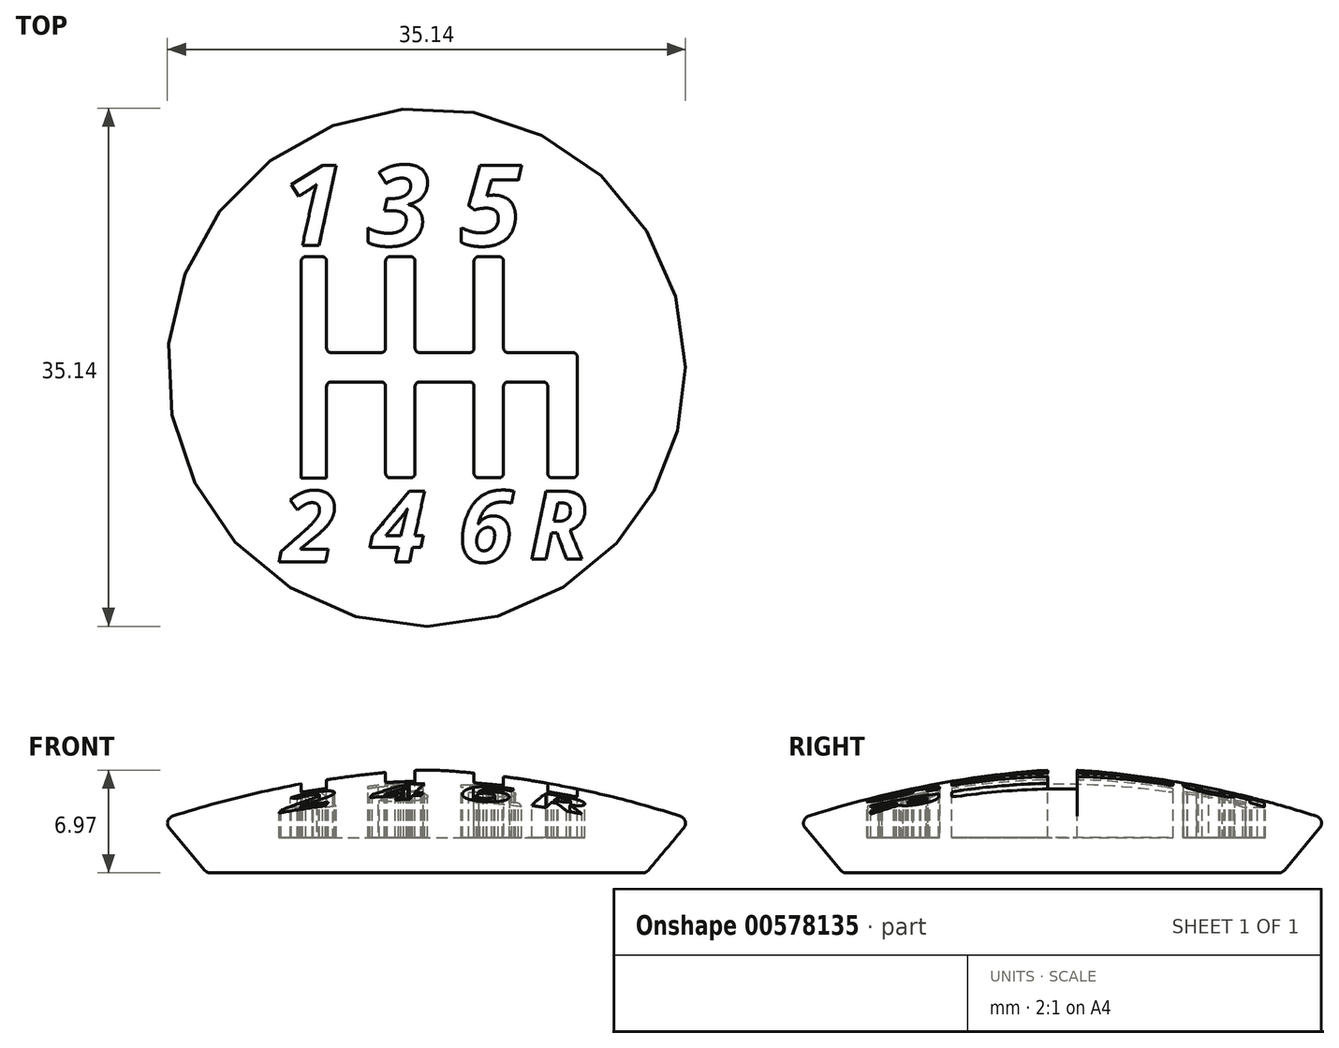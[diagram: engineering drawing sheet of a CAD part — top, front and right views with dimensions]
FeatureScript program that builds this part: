
annotation { "Feature Type Name" : "Feature", "Feature Type Description" : "" }
export const myFeature = defineFeature(function(context is Context, id is Id, definition is map)
    precondition{}
    {
        {
            var Q0;
            Q0=qCreatedBy(makeId("Front.planeOp"),FACE);
            var sketch = newSketch(context, id + "F0", { "sketchPlane" : qUnion([Q0])});
            skLineSegment(sketch, "E0", {"start": v(0, 0) * mm, "end": v(0, 7.03) * mm});
            skLineSegment(sketch, "E1", {"start": v(0, 0) * mm, "end": v(-14.9, 0) * mm});
            skLineSegment(sketch, "E2", {"start": v(-14.9, 0) * mm, "end": v(-17.93, 3.61) * mm});
            skArc(sketch, "E3", {"start": v(0, 7.03) * mm, "mid": v(-9.08, 5.93) * mm, "end": v(-17.93, 3.61) * mm});
            skPoint(sketch, "E3.third.point", {"position": v(25.22, 3.61) * mm});
            skLineSegment(sketch, "E4", {"start": v(-17.93, 3.61) * mm, "end": v(-17.93, 14.45) * mm, "construction": true});
            skSolve(sketch);
        }
        {
            var Q0;
            Q0=makeQuery(id+"F0.imprint","IMPRINT",FACE,{"disambiguationData":[TD([[makeQuery(id+"F0.imprint","IMPRINT",EDGE,{"derivedFrom":sQuery(id+"F0.wireOp",EDGE,"E0")}),1.0]])]});
            var Q1;
            Q1=sQuery(id+"F0.wireOp",EDGE,"E0");
            revolve(context, id + "F1", {"entities" : qUnion([Q0]), "axis" : qUnion([Q1]), "revolveType" : RevolveType.FULL});
        }
        {
            var Q0;
            Q0=qCreatedBy(makeId("Top.planeOp"),FACE);
            cPlane(context, id + "F2", {"entities" : qUnion([Q0]), "cplaneType" : CPlaneType.OFFSET, "offset" : 24.9 * mm, "width" : 152.4 * mm, "height" : 152.4 * mm});
        }
        {
            var Q0;
            Q0=qCreatedBy(id+"F2.planeOp",FACE);
            var sketch = newSketch(context, id + "F3", { "sketchPlane" : qUnion([Q0])});
            skLineSegment(sketch, "E5", {"start": v(-8.5, 7.2) * mm, "end": v(-8.5, -7.5) * mm});
            skLineSegment(sketch, "E6", {"start": v(-9.44, -7.5) * mm, "end": v(-6.78, -7.5) * mm});
            skLineSegment(sketch, "E7", {"start": v(-6.78, -7.5) * mm, "end": v(-6.78, -1.3) * mm});
            skLineSegment(sketch, "E8", {"start": v(-6.48, -1) * mm, "end": v(-3.08, -1) * mm});
            skLineSegment(sketch, "E9", {"start": v(-2.78, -1.3) * mm, "end": v(-2.78, -7.2) * mm});
            skLineSegment(sketch, "E10", {"start": v(-2.48, -7.5) * mm, "end": v(-1.08, -7.5) * mm});
            skLineSegment(sketch, "E11", {"start": v(-0.78, -7.2) * mm, "end": v(-0.78, -1.3) * mm});
            skLineSegment(sketch, "E12", {"start": v(-0.48, -1) * mm, "end": v(2.92, -1) * mm});
            skLineSegment(sketch, "E13", {"start": v(3.22, -1.3) * mm, "end": v(3.22, -7.2) * mm});
            skLineSegment(sketch, "E14", {"start": v(3.52, -7.5) * mm, "end": v(4.92, -7.5) * mm});
            skLineSegment(sketch, "E15", {"start": v(5.22, -7.2) * mm, "end": v(5.22, -1.3) * mm});
            skLineSegment(sketch, "E16", {"start": v(5.52, -1) * mm, "end": v(7.92, -1) * mm});
            skLineSegment(sketch, "E17", {"start": v(8.22, -1.3) * mm, "end": v(8.22, -7.2) * mm});
            skLineSegment(sketch, "E18", {"start": v(8.52, -7.5) * mm, "end": v(9.92, -7.5) * mm});
            skLineSegment(sketch, "E19", {"start": v(10.22, -7.2) * mm, "end": v(10.22, 0.7) * mm});
            skLineSegment(sketch, "E20", {"start": v(9.92, 1) * mm, "end": v(5.52, 1) * mm});
            skLineSegment(sketch, "E21", {"start": v(5.22, 1.3) * mm, "end": v(5.22, 7.2) * mm});
            skLineSegment(sketch, "E22", {"start": v(4.92, 7.5) * mm, "end": v(3.52, 7.5) * mm});
            skLineSegment(sketch, "E23", {"start": v(3.22, 7.2) * mm, "end": v(3.22, 1.3) * mm});
            skLineSegment(sketch, "E24", {"start": v(2.92, 1) * mm, "end": v(-0.48, 1) * mm});
            skLineSegment(sketch, "E25", {"start": v(-0.78, 1.3) * mm, "end": v(-0.78, 7.2) * mm});
            skLineSegment(sketch, "E26", {"start": v(-1.08, 7.5) * mm, "end": v(-2.48, 7.5) * mm});
            skLineSegment(sketch, "E27", {"start": v(-2.78, 7.2) * mm, "end": v(-2.78, 1.3) * mm});
            skLineSegment(sketch, "E28", {"start": v(-3.08, 1) * mm, "end": v(-6.48, 1) * mm});
            skLineSegment(sketch, "E29", {"start": v(-6.78, 1.3) * mm, "end": v(-6.78, 7.2) * mm});
            skLineSegment(sketch, "E30", {"start": v(-7.08, 7.5) * mm, "end": v(-8.2, 7.5) * mm});
            skPoint(sketch, "E31.visualSharp", {"position": v(-8.78, 7.5) * mm});
            skArc(sketch, "E31.filletArc", {"start": v(-8.2, 7.5) * mm, "mid": v(-8.4, 7.41) * mm, "end": v(-8.5, 7.2) * mm});
            skPoint(sketch, "E32.visualSharp", {"position": v(-6.78, 7.5) * mm});
            skArc(sketch, "E32.filletArc", {"start": v(-6.78, 7.2) * mm, "mid": v(-6.86, 7.41) * mm, "end": v(-7.08, 7.5) * mm});
            skPoint(sketch, "E33.visualSharp", {"position": v(-6.78, 1) * mm});
            skArc(sketch, "E33.filletArc", {"start": v(-6.78, 1.3) * mm, "mid": v(-6.69, 1.09) * mm, "end": v(-6.48, 1) * mm});
            skPoint(sketch, "E34.visualSharp", {"position": v(-2.78, 1) * mm});
            skArc(sketch, "E34.filletArc", {"start": v(-3.08, 1) * mm, "mid": v(-2.86, 1.09) * mm, "end": v(-2.78, 1.3) * mm});
            skPoint(sketch, "E35.visualSharp", {"position": v(-2.78, 7.5) * mm});
            skArc(sketch, "E35.filletArc", {"start": v(-2.48, 7.5) * mm, "mid": v(-2.69, 7.41) * mm, "end": v(-2.78, 7.2) * mm});
            skPoint(sketch, "E36.visualSharp", {"position": v(-0.78, 7.5) * mm});
            skArc(sketch, "E36.filletArc", {"start": v(-0.78, 7.2) * mm, "mid": v(-0.86, 7.41) * mm, "end": v(-1.08, 7.5) * mm});
            skPoint(sketch, "E37.visualSharp", {"position": v(-0.78, 1) * mm});
            skArc(sketch, "E37.filletArc", {"start": v(-0.78, 1.3) * mm, "mid": v(-0.69, 1.09) * mm, "end": v(-0.48, 1) * mm});
            skPoint(sketch, "E38.visualSharp", {"position": v(3.22, 1) * mm});
            skArc(sketch, "E38.filletArc", {"start": v(2.92, 1) * mm, "mid": v(3.14, 1.09) * mm, "end": v(3.22, 1.3) * mm});
            skPoint(sketch, "E39.visualSharp", {"position": v(3.22, 7.5) * mm});
            skArc(sketch, "E39.filletArc", {"start": v(3.52, 7.5) * mm, "mid": v(3.31, 7.41) * mm, "end": v(3.22, 7.2) * mm});
            skPoint(sketch, "E40.visualSharp", {"position": v(5.22, 7.5) * mm});
            skArc(sketch, "E40.filletArc", {"start": v(5.22, 7.2) * mm, "mid": v(5.14, 7.41) * mm, "end": v(4.92, 7.5) * mm});
            skPoint(sketch, "E41.visualSharp", {"position": v(5.22, 1) * mm});
            skArc(sketch, "E41.filletArc", {"start": v(5.22, 1.3) * mm, "mid": v(5.31, 1.09) * mm, "end": v(5.52, 1) * mm});
            skPoint(sketch, "E42.visualSharp", {"position": v(10.22, 1) * mm});
            skArc(sketch, "E42.filletArc", {"start": v(10.22, 0.7) * mm, "mid": v(10.14, 0.91) * mm, "end": v(9.92, 1) * mm});
            skPoint(sketch, "E43.visualSharp", {"position": v(10.22, -7.5) * mm});
            skArc(sketch, "E43.filletArc", {"start": v(9.92, -7.5) * mm, "mid": v(10.14, -7.41) * mm, "end": v(10.22, -7.2) * mm});
            skPoint(sketch, "E44.visualSharp", {"position": v(8.22, -7.5) * mm});
            skArc(sketch, "E44.filletArc", {"start": v(8.22, -7.2) * mm, "mid": v(8.31, -7.41) * mm, "end": v(8.52, -7.5) * mm});
            skPoint(sketch, "E45.visualSharp", {"position": v(8.22, -1) * mm});
            skArc(sketch, "E45.filletArc", {"start": v(8.22, -1.3) * mm, "mid": v(8.14, -1.09) * mm, "end": v(7.92, -1) * mm});
            skPoint(sketch, "E46.visualSharp", {"position": v(5.22, -1) * mm});
            skArc(sketch, "E46.filletArc", {"start": v(5.52, -1) * mm, "mid": v(5.31, -1.09) * mm, "end": v(5.22, -1.3) * mm});
            skPoint(sketch, "E47.visualSharp", {"position": v(5.22, -7.5) * mm});
            skArc(sketch, "E47.filletArc", {"start": v(4.92, -7.5) * mm, "mid": v(5.14, -7.41) * mm, "end": v(5.22, -7.2) * mm});
            skPoint(sketch, "E48.visualSharp", {"position": v(3.22, -7.5) * mm});
            skArc(sketch, "E48.filletArc", {"start": v(3.22, -7.2) * mm, "mid": v(3.31, -7.41) * mm, "end": v(3.52, -7.5) * mm});
            skPoint(sketch, "E49.visualSharp", {"position": v(3.22, -1) * mm});
            skArc(sketch, "E49.filletArc", {"start": v(3.22, -1.3) * mm, "mid": v(3.14, -1.09) * mm, "end": v(2.92, -1) * mm});
            skPoint(sketch, "E50.visualSharp", {"position": v(-0.78, -1) * mm});
            skArc(sketch, "E50.filletArc", {"start": v(-0.48, -1) * mm, "mid": v(-0.69, -1.09) * mm, "end": v(-0.78, -1.3) * mm});
            skPoint(sketch, "E51.visualSharp", {"position": v(-0.78, -7.5) * mm});
            skArc(sketch, "E51.filletArc", {"start": v(-1.08, -7.5) * mm, "mid": v(-0.86, -7.41) * mm, "end": v(-0.78, -7.2) * mm});
            skPoint(sketch, "E52.visualSharp", {"position": v(-2.78, -7.5) * mm});
            skArc(sketch, "E52.filletArc", {"start": v(-2.78, -7.2) * mm, "mid": v(-2.69, -7.41) * mm, "end": v(-2.48, -7.5) * mm});
            skPoint(sketch, "E53.visualSharp", {"position": v(-2.78, -1) * mm});
            skArc(sketch, "E53.filletArc", {"start": v(-2.78, -1.3) * mm, "mid": v(-2.86, -1.09) * mm, "end": v(-3.08, -1) * mm});
            skPoint(sketch, "E54.visualSharp", {"position": v(-6.78, -1) * mm});
            skArc(sketch, "E54.filletArc", {"start": v(-6.48, -1) * mm, "mid": v(-6.69, -1.09) * mm, "end": v(-6.78, -1.3) * mm});
            skPoint(sketch, "E55.visualSharp", {"position": v(-6.78, -7.5) * mm});
            skArc(sketch, "E55.filletArc", {"start": v(-6.78, -7.5) * mm, "mid": v(-7.37, -7.46) * mm, "end": v(-6.8, -7.6) * mm});
            skPoint(sketch, "E56.visualSharp", {"position": v(-8.2, -7.5) * mm});
            skArc(sketch, "E56.filletArc", {"start": v(-8.5, -7.5) * mm, "mid": v(-8.37, -7.5) * mm, "end": v(-8.25, -7.44) * mm});
            skLineSegment(sketch, "E57", {"start": v(-19.99, 0) * mm, "end": v(21.16, 0) * mm, "construction": true});
            skText(sketch, "E58", { "text": "1", "fontName": "OpenSans-BoldItalic.ttf"});
            skText(sketch, "E59", { "text": "3", "fontName": "OpenSans-BoldItalic.ttf"});
            skText(sketch, "E60", { "text": "5", "fontName": "OpenSans-BoldItalic.ttf"});
            skText(sketch, "E61", { "text": "4", "fontName": "OpenSans-BoldItalic.ttf"});
            skText(sketch, "E62", { "text": "6", "fontName": "OpenSans-BoldItalic.ttf"});
            skText(sketch, "E63", { "text": "R", "fontName": "OpenSans-BoldItalic.ttf"});
            skText(sketch, "E64", { "text": "2", "fontName": "OpenSans-BoldItalic.ttf"});
            const initialGuessF3  = {"E58": [-0.00984, 0.00825, 1, 0, 0.00548], "E59": [-0.00403, 0.00825, 1, 0, 0.00548], "E60": [0.00225, 0.00825, 1, 0, 0.00548], "E61": [-0.00376, -0.0132, 1, 0, 0.00484], "E62": [0.00215, -0.0132, 1, 0, 0.00484], "E63": [0.00697, -0.01302, 1, 0, 0.00466], "E64": [-0.00984, -0.0132, 1, 0, 0.00484]};
            skSetInitialGuess(sketch, initialGuessF3);
            skSolve(sketch);
        }
        {
            var Q0;
            Q0 = qSketchRegion(id + "F3", true);
            extrude(context, id + "F4", {"entities" : qUnion([Q0]), "operationType" : NewBodyOperationType.REMOVE, "oppositeDirection" : true, "depth" : 22.5 * mm, "offsetDistance" : 25 * mm});
        }
        {
            var Q0;
            Q0=makeQuery(id+"F1.opRevolve","SWEPT_EDGE",EDGE,{"disambiguationData":[OSD([sQuery(id+"F0.wireOp",EDGE,"E2"),sQuery(id+"F0.wireOp",EDGE,"E3")])]});
            var Q1;
            Q1=makeQuery(id+"F1.opRevolve","SWEPT_EDGE",EDGE,{"disambiguationData":[OSD([sQuery(id+"F0.wireOp",EDGE,"E1"),sQuery(id+"F0.wireOp",EDGE,"E2")])]});
            fillet(context, id + "F5", {"entities" : qUnion([Q0, Q1]), "radius" : 0.5 * mm, "tangentPropagation" : true, "allowEdgeOverflow" : false});
        }
    });
